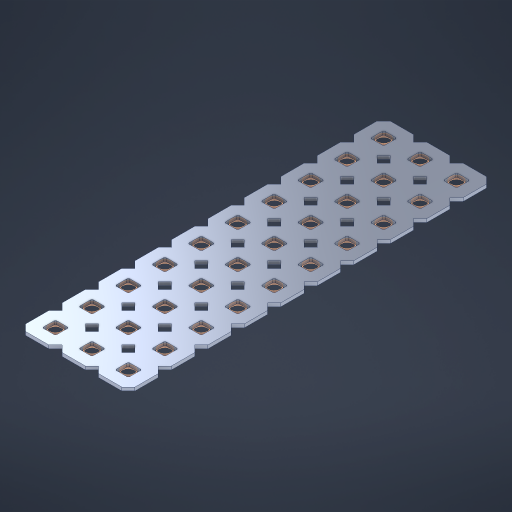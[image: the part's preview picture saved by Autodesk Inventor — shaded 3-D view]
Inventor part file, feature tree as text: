
AUTODESK INVENTOR PART (.ipt)
format: ipt  version: 2023 (Build 270158000, 158)  size: 603,136 bytes
history: native  units: in
note: dims shown in document units (in); Inventor stores cm internally (conversion verified against a paired STEP export)
features: other x31, extrude x29, sketch x2, pattern_linear x1
ambient origin geometry x8: Origin, YZ Plane, XZ Plane, XY Plane, X Axis, Y Axis, Z Axis, Center Point
bodies: Solid1 (feature_tree), Body (feature_tree)
feature tree (63):
  pattern_linear  "Rectangular Pattern1"  Spacing1=0.09in  [1 undecoded]
  sketch  "Sketch1"  dims[d1=0.5in]
  sketch  "Sketch2"  dims[d2=0.182in d3=0.09in d4=0.09in d5=0.09in d6=0.09in d7=0.09in d8=0.09in d9=0.09in d10=0.09in d11=0.02in d13=0.0in d14=0.172in d15=0.0625in d16=0.0in d19=0.5in d22=0.5in]
  other  "Srf1"
  other  "Srf126"
  other  "Srf127"
  other  "Srf128"
  other  "Srf129"
  other  "Srf130"
  other  "Srf131"
  other  "Srf250"
  other  "Srf251"
  other  "Srf252"
  other  "Srf268"
  other  "Srf269"
  other  "Srf270"
  other  "Srf271"
  other  "Srf272"
  other  "Srf273"
  other  "Srf274"
  other  "Srf275"
  other  "Srf276"
  other  "Srf277"
  other  "Srf293"
  other  "Srf294"
  other  "Srf295"
  other  "Srf296"
  other  "Srf297"
  other  "Srf298"
  other  "Srf299"
  other  "Srf300"
  other  "Srf301"
  other  "Srf302"
  other  "Circle"
  extrude  "ExtrusionSrf126"  Depth=0.09in
  extrude  "ExtrusionSrf127"  Depth=0.09in
  extrude  "ExtrusionSrf128"  Depth=0.09in
  extrude  "ExtrusionSrf129"  Depth=0.09in
  extrude  "ExtrusionSrf130"  Depth=0.09in
  extrude  "ExtrusionSrf131"  Depth=0.09in
  extrude  "ExtrusionSrf250"  Depth=0.09in
  extrude  "ExtrusionSrf251"  Depth=0.02in
  extrude  "ExtrusionSrf252"  TaperAngle=0.0deg  [1 undecoded]
  extrude  "ExtrusionSrf268"  Depth=0.5in
  extrude  "ExtrusionSrf269"  Depth=0.5in TaperAngle=0.0deg
  extrude  "ExtrusionSrf270"  Depth=0.5in
  extrude  "ExtrusionSrf271"  Depth=0.5in
  extrude  "ExtrusionSrf272"  [1 undecoded]
  extrude  "ExtrusionSrf273"  [1 undecoded]
  extrude  "ExtrusionSrf274"  [1 undecoded]
  extrude  "ExtrusionSrf275"  [1 undecoded]
  extrude  "ExtrusionSrf276"  [1 undecoded]
  extrude  "ExtrusionSrf277"  [1 undecoded]
  extrude  "ExtrusionSrf293"  [1 undecoded]
  extrude  "ExtrusionSrf294"  [1 undecoded]
  extrude  "ExtrusionSrf295"  [1 undecoded]
  extrude  "ExtrusionSrf296"  [1 undecoded]
  extrude  "ExtrusionSrf297"  [1 undecoded]
  extrude  "ExtrusionSrf298"  [1 undecoded]
  extrude  "ExtrusionSrf299"  [1 undecoded]
  extrude  "ExtrusionSrf300"  [1 undecoded]
  extrude  "ExtrusionSrf301"  [1 undecoded]
  extrude  "ExtrusionSrf302"  [1 undecoded]
note: 18 required parameter values undecoded (feature->parameter linkage not recoverable at this tier; creation-order binding heuristic only, values carry confidence <= 0.55)
